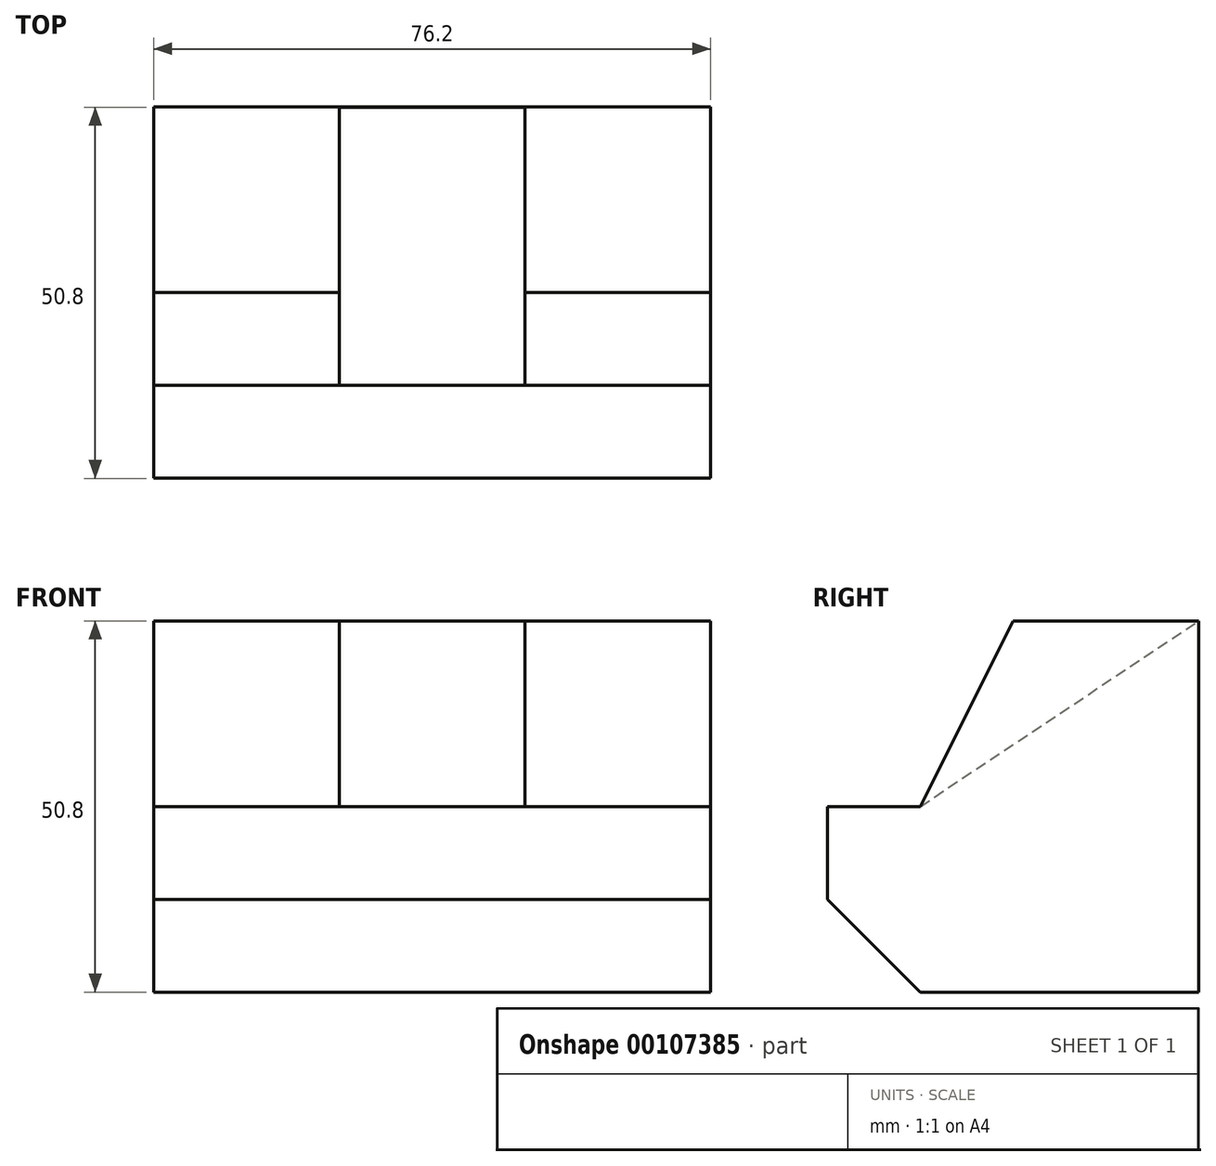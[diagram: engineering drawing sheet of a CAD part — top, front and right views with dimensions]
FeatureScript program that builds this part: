
annotation { "Feature Type Name" : "Feature", "Feature Type Description" : "" }
export const myFeature = defineFeature(function(context is Context, id is Id, definition is map)
    precondition{}
    {
        {
            var Q0;
            Q0=qCreatedBy(makeId("Right.planeOp"),FACE);
            var sketch = newSketch(context, id + "F0", { "sketchPlane" : qUnion([Q0])});
            skLineSegment(sketch, "E0", {"start": v(-11.88, 16.82) * mm, "end": v(13.52, 16.82) * mm});
            skLineSegment(sketch, "E1", {"start": v(13.52, 16.82) * mm, "end": v(13.52, -33.98) * mm});
            skLineSegment(sketch, "E2", {"start": v(13.52, -33.98) * mm, "end": v(-24.58, -33.98) * mm});
            skLineSegment(sketch, "E3", {"start": v(-24.58, -33.98) * mm, "end": v(-24.58, -8.58) * mm});
            skLineSegment(sketch, "E4", {"start": v(-24.58, -8.58) * mm, "end": v(-11.88, 16.82) * mm});
            skSolve(sketch);
        }
        {
            var Q0;
            Q0=makeQuery(id+"F0.imprint","IMPRINT",FACE,{"disambiguationData":[TD([[makeQuery(id+"F0.imprint","IMPRINT",EDGE,{"derivedFrom":sQuery(id+"F0.wireOp",EDGE,"E0")}),-1.0]])]});
            extrude(context, id + "F1", {"entities" : qUnion([Q0]), "oppositeDirection" : true, "depth" : 76.2 * mm});
        }
        {
            var Q0;
            Q0=makeQuery(id+"F1.opExtrude","CAP_FACE",FACE,{"disambiguationData":[OSD([sQuery(id+"F0.wireOp",EDGE,"E0"),sQuery(id+"F0.wireOp",EDGE,"E1"),sQuery(id+"F0.wireOp",EDGE,"E2"),sQuery(id+"F0.wireOp",EDGE,"E3"),sQuery(id+"F0.wireOp",EDGE,"E4")])],"isStart":true});
            var sketch = newSketch(context, id + "F2", { "sketchPlane" : qUnion([Q0])});
            skLineSegment(sketch, "E5", {"start": v(-24.58, -8.58) * mm, "end": v(-37.28, -8.58) * mm});
            skLineSegment(sketch, "E6", {"start": v(-37.28, -8.58) * mm, "end": v(-37.28, -21.28) * mm});
            skLineSegment(sketch, "E7", {"start": v(-37.28, -21.28) * mm, "end": v(-24.58, -33.98) * mm});
            skLineSegment(sketch, "E8", {"start": v(-24.58, -8.58) * mm, "end": v(-24.58, -33.98) * mm});
            skSolve(sketch);
        }
        {
            var Q0;
            Q0 = qSketchRegion(id + "F2", true);
            extrude(context, id + "F3", {"entities" : qUnion([Q0]), "operationType" : NewBodyOperationType.ADD, "oppositeDirection" : true, "depth" : 76.2 * mm});
        }
        {
            var Q0;
            {var subQ0=sQuery(id+"F0.wireOp",EDGE,"E4");Q0=makeQuery(id+"F3.boolean.opBoolean","MERGE",EDGE,{"derivedFrom":[makeQuery(id+"F1.opExtrude","SWEPT_EDGE",EDGE,{"disambiguationData":[OSD([sQuery(id+"F0.wireOp",EDGE,"E3"),subQ0])]}),makeQuery(id+"F3.opExtrude","SWEPT_EDGE",EDGE,{"disambiguationData":[OSD([subQ0,sQuery(id+"F2.wireOp",EDGE,"E5"),sQuery(id+"F2.wireOp",EDGE,"E8")])]})]});}
            var Q1;
            Q1=makeQuery(id+"F1.opExtrude","SWEPT_EDGE",EDGE,{"disambiguationData":[OSD([sQuery(id+"F0.wireOp",EDGE,"E0"),sQuery(id+"F0.wireOp",EDGE,"E1")])]});
            cPlane(context, id + "F4", {"entities" : qUnion([Q0, Q1]), "cplaneType" : CPlaneType.LINE_ANGLE, "offset" : 25.4 * mm, "angle" : 0 * degree, "width" : 152.4 * mm, "height" : 152.4 * mm});
        }
        {
            var Q0;
            Q0=qCreatedBy(id+"F4.planeOp",FACE);
            var sketch = newSketch(context, id + "F5", { "sketchPlane" : qUnion([Q0])});
            skLineSegment(sketch, "E9", {"start": v(-50.8, -25.21) * mm, "end": v(-50.8, 20.58) * mm});
            skLineSegment(sketch, "E10", {"start": v(-50.8, 20.58) * mm, "end": v(-25.4, 20.58) * mm});
            skLineSegment(sketch, "E11", {"start": v(-50.8, -25.21) * mm, "end": v(-25.4, -25.21) * mm});
            skLineSegment(sketch, "E12", {"start": v(-25.4, -25.21) * mm, "end": v(-25.4, 20.58) * mm});
            skSolve(sketch);
        }
        {
            var Q0;
            Q0 = qSketchRegion(id + "F5", true);
            extrude(context, id + "F6", {"entities" : qUnion([Q0]), "operationType" : NewBodyOperationType.REMOVE, "depth" : 25.4 * mm});
        }
    });
